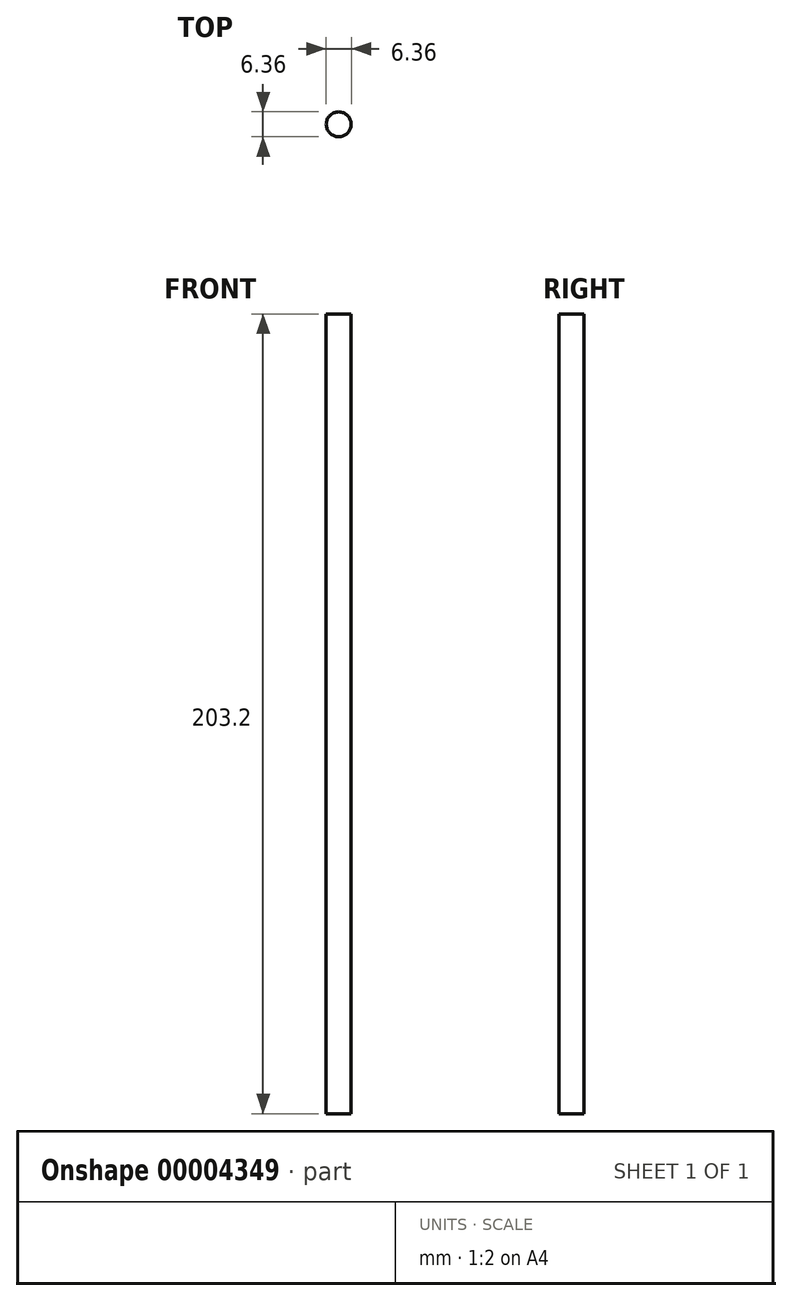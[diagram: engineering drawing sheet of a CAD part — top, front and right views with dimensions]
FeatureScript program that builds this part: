
annotation { "Feature Type Name" : "Feature", "Feature Type Description" : "" }
export const myFeature = defineFeature(function(context is Context, id is Id, definition is map)
    precondition{}
    {
        {
            var Q0;
            Q0=qCreatedBy(makeId("Top.planeOp"),FACE);
            var sketch = newSketch(context, id + "F0", { "sketchPlane" : qUnion([Q0])});
            skCircle(sketch, "E0", {"center": v(0, 0) * mm, "radius": 3.17 * mm});
            skSolve(sketch);
        }
        {
            var Q0;
            Q0=makeQuery(id+"F0.imprint","IMPRINT",FACE,{"disambiguationData":[TD([[makeQuery(id+"F0.imprint","IMPRINT",EDGE,{"derivedFrom":sQuery(id+"F0.wireOp",EDGE,"E0")}),1.0]])]});
            extrude(context, id + "F1", {"entities" : qUnion([Q0]), "depth" : 203.2 * mm});
        }
    });
